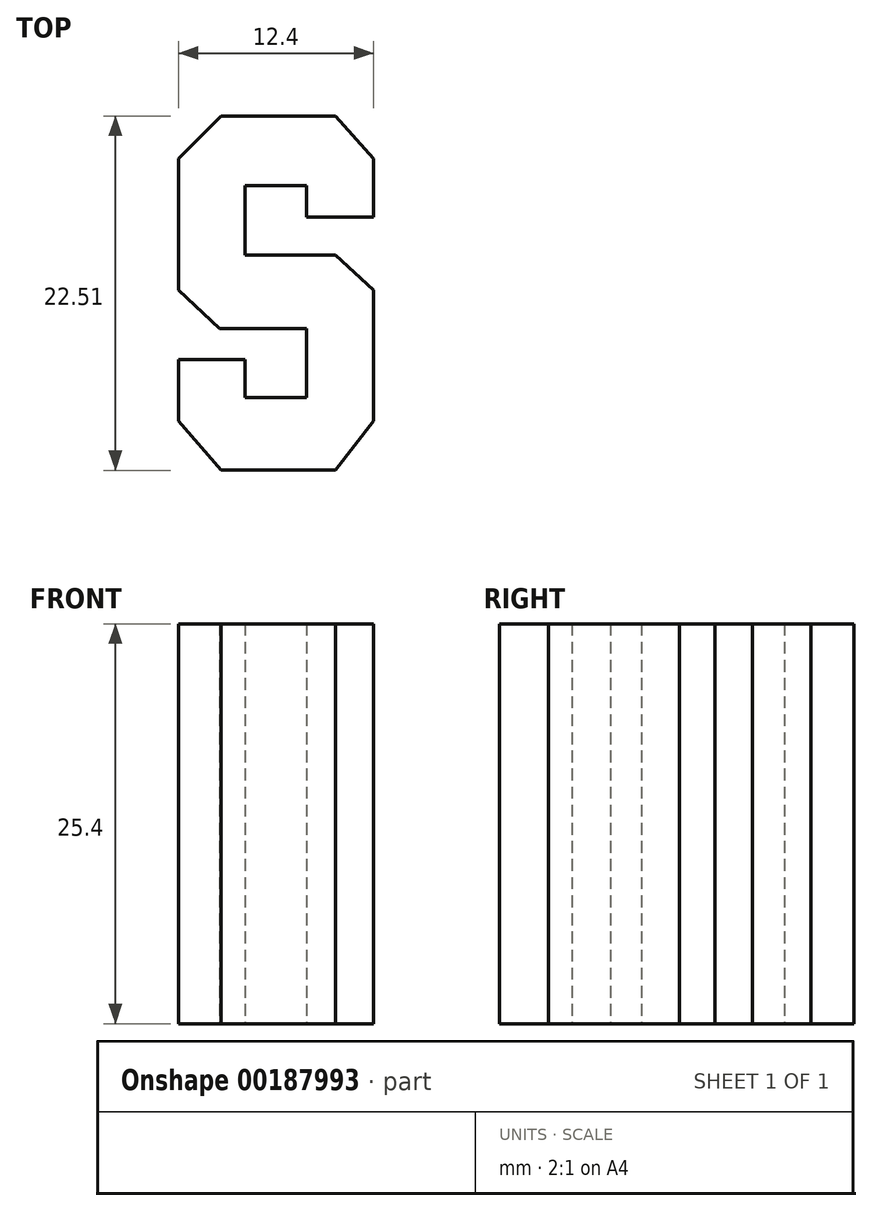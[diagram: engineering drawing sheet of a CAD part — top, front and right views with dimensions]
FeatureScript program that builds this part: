
annotation { "Feature Type Name" : "Feature", "Feature Type Description" : "" }
export const myFeature = defineFeature(function(context is Context, id is Id, definition is map)
    precondition{}
    {
        {
            var Q0;
            Q0=qCreatedBy(makeId("Top.planeOp"),FACE);
            var sketch = newSketch(context, id + "F0", { "sketchPlane" : qUnion([Q0])});
            skLineSegment(sketch, "E0", {"start": v(9.98, 0) * mm, "end": v(12.4, -2.72) * mm});
            skLineSegment(sketch, "E1", {"start": v(12.4, -2.72) * mm, "end": v(12.4, -6.43) * mm});
            skLineSegment(sketch, "E2", {"start": v(12.4, -6.43) * mm, "end": v(8.15, -6.43) * mm});
            skLineSegment(sketch, "E3", {"start": v(8.15, -6.43) * mm, "end": v(8.15, -4.42) * mm});
            skLineSegment(sketch, "E4", {"start": v(8.15, -4.42) * mm, "end": v(4.24, -4.42) * mm});
            skLineSegment(sketch, "E5", {"start": v(4.24, -4.42) * mm, "end": v(4.24, -8.83) * mm});
            skLineSegment(sketch, "E6", {"start": v(4.24, -8.83) * mm, "end": v(9.98, -8.83) * mm});
            skLineSegment(sketch, "E7", {"start": v(9.98, -8.83) * mm, "end": v(12.4, -11.07) * mm});
            skLineSegment(sketch, "E8", {"start": v(12.4, -11.07) * mm, "end": v(12.4, -19.4) * mm});
            skLineSegment(sketch, "E9", {"start": v(12.4, -19.4) * mm, "end": v(9.98, -22.5) * mm});
            skLineSegment(sketch, "E10", {"start": v(0, -19.4) * mm, "end": v(0, -15.47) * mm});
            skLineSegment(sketch, "E11", {"start": v(0, -15.47) * mm, "end": v(4.24, -15.47) * mm});
            skLineSegment(sketch, "E12", {"start": v(4.24, -15.47) * mm, "end": v(4.24, -17.9) * mm});
            skLineSegment(sketch, "E13", {"start": v(4.24, -17.9) * mm, "end": v(8.16, -17.9) * mm});
            skLineSegment(sketch, "E14", {"start": v(8.16, -17.9) * mm, "end": v(8.16, -13.5) * mm});
            skLineSegment(sketch, "E15", {"start": v(0, -11.07) * mm, "end": v(0, -2.72) * mm});
            skPoint(sketch, "E16.orphan", {"position": v(0, 0) * mm});
            skLineSegment(sketch, "E17", {"start": v(0, -2.72) * mm, "end": v(2.73, 0) * mm});
            skLineSegment(sketch, "E18", {"start": v(2.73, 0) * mm, "end": v(9.98, 0) * mm});
            skLineSegment(sketch, "E19", {"start": v(9.98, -22.5) * mm, "end": v(2.73, -22.5) * mm});
            skLineSegment(sketch, "E20", {"start": v(2.73, -22.5) * mm, "end": v(0, -19.4) * mm});
            skLineSegment(sketch, "E21", {"start": v(0, -11.07) * mm, "end": v(2.63, -13.5) * mm});
            skPoint(sketch, "E22.end.orphan", {"position": v(4.24, -13.5) * mm});
            skLineSegment(sketch, "E23", {"start": v(2.63, -13.5) * mm, "end": v(8.16, -13.5) * mm});
            skSolve(sketch);
        }
        {
            var Q0;
            Q0 = qSketchRegion(id + "F0", true);
            extrude(context, id + "F1", {"entities" : qUnion([Q0]), "depth" : 25.4 * mm});
        }
    });
